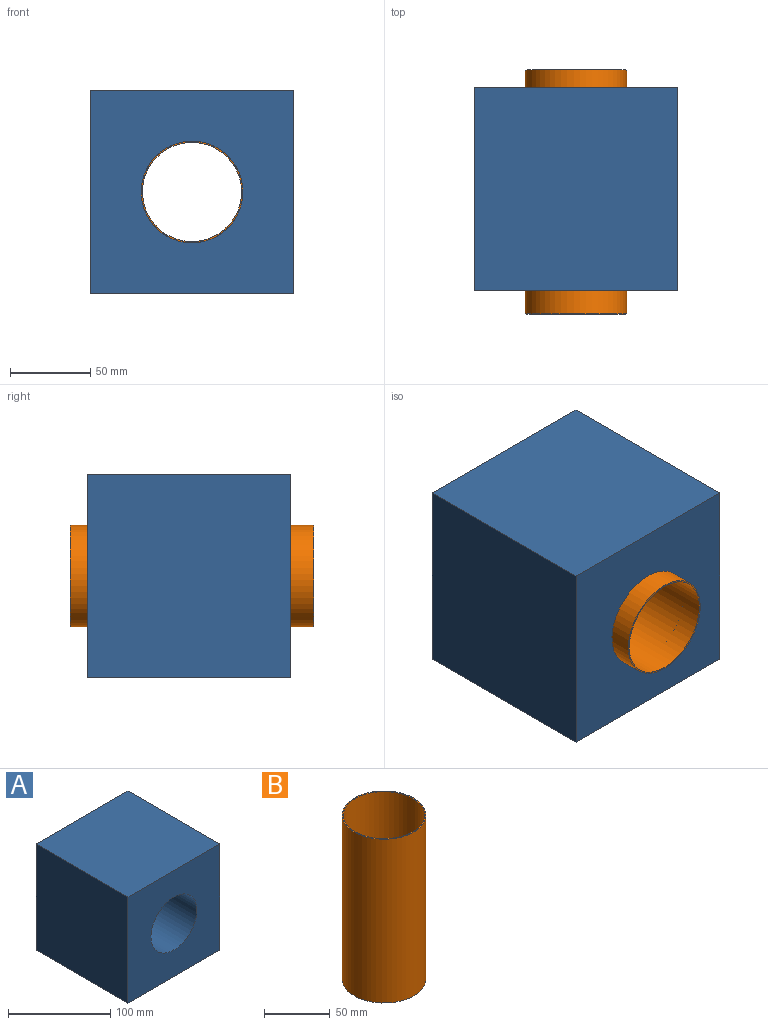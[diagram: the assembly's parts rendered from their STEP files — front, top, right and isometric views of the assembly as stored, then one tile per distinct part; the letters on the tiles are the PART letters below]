
ASSEMBLY  parts=2 mates=1
PART A: 7 faces, bbox 127x127x127 mm
  f0: plane 127x127mm, normal (1,0,0), area 16129mm2, adj f1,f3,f4,f5
  f1: plane 127x127mm, normal (0,1,0), area 12962.1mm2, adj f0,f2,f4,f5,f6
  f2: plane 127x127mm, normal (-1,0,0), area 16129mm2, adj f1,f3,f4,f5
  f3: plane 127x127mm, normal (0,-1,0), area 12962.1mm2, adj f0,f2,f4,f5,f6
  f4: plane 127x127mm, normal (0,0,1), area 16129mm2, adj f0,f1,f2,f3
  f5: plane 127x127mm, normal (0,0,-1), area 16129mm2, adj f0,f1,f2,f3
  f6: cylinder r=31.75mm len=127mm, axis (0,-1,0), area 25335.4mm2, adj f1,f3
PART B: 4 faces, bbox 63.5x63.5x152.4 mm
  f0: cylinder r=30.96mm len=152.4mm, axis (0,0,-1), area 29642.4mm2, adj f2,f3
  f1: cylinder r=31.75mm len=152.4mm, axis (0,0,-1), area 30402.4mm2, adj f2,f3
  f2: plane 63.5x63.5mm, normal (0,0,1), area 156.4mm2, adj f0,f1
  f3: plane 63.5x63.5mm, normal (0,0,-1), area 156.4mm2, adj f0,f1
PLACE A t=(23.36,40.96,-39.6)mm
PLACE B rot(axis=(0.58,-0.58,0.58),120deg) t=(-40.14,51.83,23.9)mm
MATE slider B.f0 <-> A.f6  axis (0,1,0) through (-40.14,-100.57,23.9)mm
